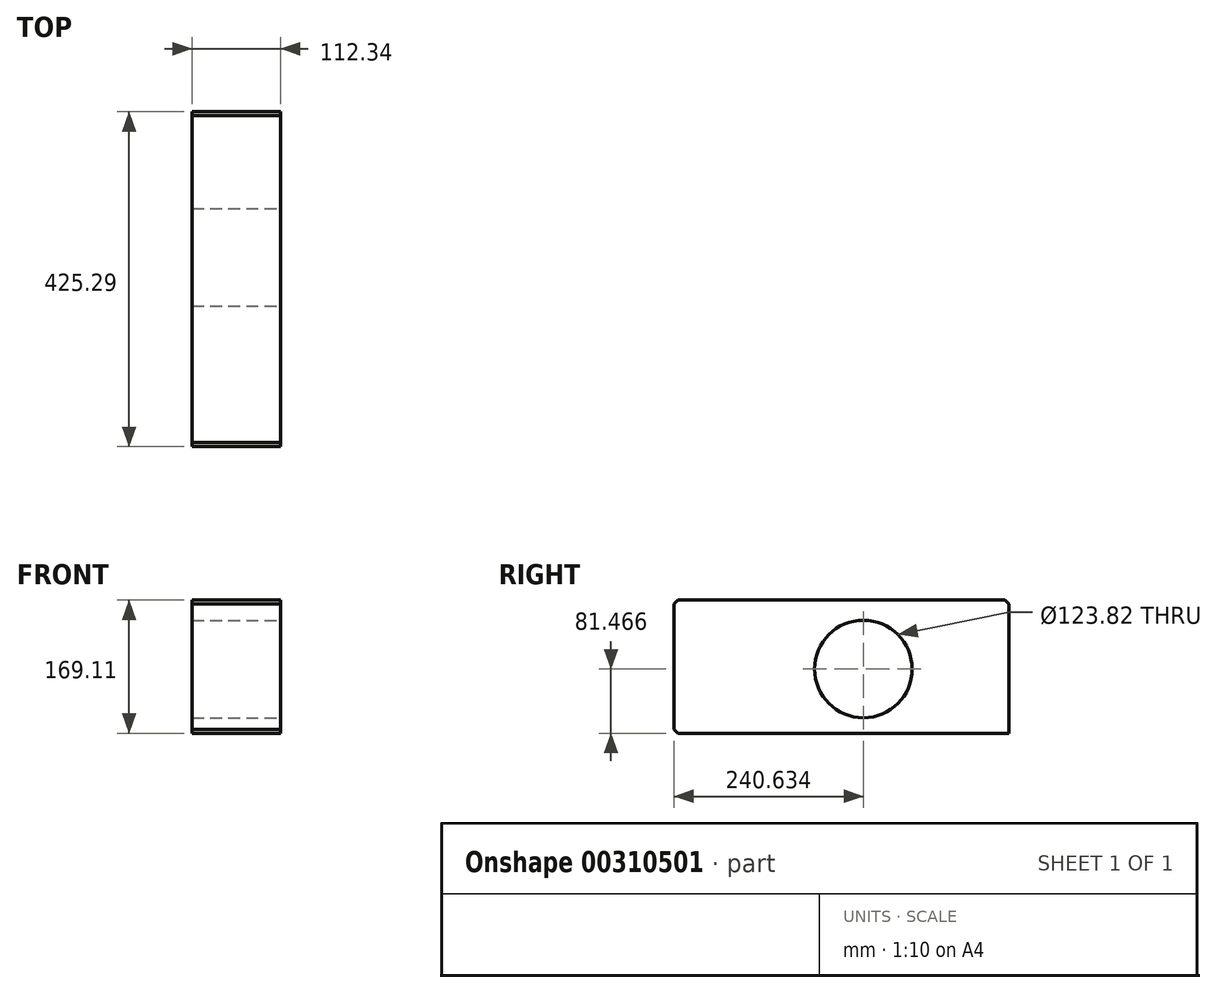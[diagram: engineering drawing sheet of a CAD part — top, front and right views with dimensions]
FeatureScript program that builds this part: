
annotation { "Feature Type Name" : "Feature", "Feature Type Description" : "" }
export const myFeature = defineFeature(function(context is Context, id is Id, definition is map)
    precondition{}
    {
        {
            var Q0;
            Q0=qCreatedBy(makeId("Front.planeOp"),FACE);
            var sketch = newSketch(context, id + "F0", { "sketchPlane" : qUnion([Q0])});
            skLineSegment(sketch, "E0.bottom", {"start": v(0, 169.1) * mm, "end": v(-112.34, 169.1) * mm});
            skLineSegment(sketch, "E0.top", {"start": v(0, 0) * mm, "end": v(-112.34, 0) * mm});
            skLineSegment(sketch, "E0.left", {"start": v(0, 169.1) * mm, "end": v(0, 0) * mm});
            skLineSegment(sketch, "E0.right", {"start": v(-112.34, 169.1) * mm, "end": v(-112.34, 0) * mm});
            skSolve(sketch);
        }
        {
            var Q0;
            Q0=makeQuery(id+"F0.imprint","IMPRINT",FACE,{"disambiguationData":[TD([[makeQuery(id+"F0.imprint","IMPRINT",EDGE,{"derivedFrom":sQuery(id+"F0.wireOp",EDGE,"E0.bottom")}),1.0]])]});
            var sketch = newSketch(context, id + "F1", { "sketchPlane" : qUnion([Q0])});
            skSolve(sketch);
        }
        {
            var Q0;
            Q0 = qSketchRegion(id + "F1", true);
            var Q1;
            Q1=makeQuery(id+"F0.imprint","IMPRINT",FACE,{"disambiguationData":[TD([[makeQuery(id+"F0.imprint","IMPRINT",EDGE,{"derivedFrom":sQuery(id+"F0.wireOp",EDGE,"E0.bottom")}),1.0]])]});
            extrude(context, id + "F2", {"entities" : qUnion([Q0, Q1]), "oppositeDirection" : true, "depth" : 425.3 * mm});
        }
        {
            var Q0;
            Q0=makeQuery(id+"F2.opExtrude","SWEPT_FACE",FACE,{"disambiguationData":[OSD([sQuery(id+"F0.wireOp",EDGE,"E0.left")])]});
            var sketch = newSketch(context, id + "F3", { "sketchPlane" : qUnion([Q0])});
            skCircle(sketch, "E1", {"center": v(240.63, 81.47) * mm, "radius": 61.9 * mm});
            skSolve(sketch);
        }
        {
            var Q0;
            Q0=makeQuery(id+"F3.imprint","IMPRINT",FACE,{"disambiguationData":[TD([[makeQuery(id+"F3.imprint","IMPRINT",EDGE,{"derivedFrom":sQuery(id+"F3.wireOp",EDGE,"E1")}),1.0]])]});
            var Q1;
            Q1=sQuery(id+"F3.wireOp",EDGE,"E1");
            extrude(context, id + "F4", {"entities" : qUnion([Q0]), "operationType" : NewBodyOperationType.REMOVE, "surfaceEntities" : qUnion([Q1]), "oppositeDirection" : true, "depth" : 148.8 * mm});
        }
        {
            var Q0;
            Q0=makeQuery(id+"F2.opExtrude","CAP_EDGE",EDGE,{"disambiguationData":[OSD([sQuery(id+"F0.wireOp",EDGE,"E0.bottom")])],"isStart":false});
            var Q1;
            Q1=makeQuery(id+"F2.opExtrude","CAP_EDGE",EDGE,{"disambiguationData":[OSD([sQuery(id+"F0.wireOp",EDGE,"E0.bottom")])],"isStart":true});
            var Q2;
            Q2=makeQuery(id+"F2.opExtrude","CAP_EDGE",EDGE,{"disambiguationData":[OSD([sQuery(id+"F0.wireOp",EDGE,"E0.top")])],"isStart":true});
            chamfer(context, id + "F5", {"entities" : qUnion([Q0, Q1, Q2]), "width" : 5.08 * mm, "tangentPropagation" : true});
        }
    });
